FCSTD DOCUMENT  (FreeCAD 0.21R33675 (Git))
Label: Stator
License: All rights reserved
LicenseURL: http://en.wikipedia.org/wiki/All_rights_reserved
objects: App::Link×2, Spreadsheet::Sheet×1, App::Part×1
EXTERNAL_REF file=../../Master_of_Puppets.FCStd obj=Alternator
EXTERNAL_REF file=../../Master_of_Puppets.FCStd obj=Spreadsheet
EXTERNAL_REF file=Stator_ResinCast_Circular.FCStd obj=PadBody001
EXTERNAL_REF file=Stator_ResinCast_Hexagonal.FCStd obj=Body
EXTERNAL_REF file=Stator_Coils.FCStd obj=Array

FEATURE [Spreadsheet::Sheet] Spreadsheet
  cells = A1='Inputs; A2='CalculatedWindTurbineShape; B2(CalculatedWindTurbineShape)==Master_of_Puppets#Spreadsheet.CalculatedWindTurbineShape; A3='StatorThickness; B3(StatorThickness)==Master_of_Puppets#Spreadsheet.StatorThickness; A4='MechanicalClearance; B4(MechanicalClearance)==Master_of_Puppets#Spreadsheet.MechanicalClearance; A5='MagnetThickness; B5(MagnetThickness)==Master_of_Puppets#Spreadsheet.MagnetThickness; A6='RotorDiskThickness; B6(RotorDiskThickness)==Master_of_Puppets#Spreadsheet.RotorDiskThickness; A7='CoilsAngle; B7(CoilsAngle)==Master_of_Puppets#Alternator.CoilsAngle; A8='StatorResinCast; A9='CircularStatorResinCast; B9(CircularStatorResinCast)==<<Stator_ResinCast_Circular>>#<<Stator_ResinCast>>._self; A10='HexagonalStatorResinCast; B10(HexagonalStatorResinCast)==<<Stator_ResinCast_Hexagonal>>#<<Stator_ResinCast>>._self; A11='StatorResinCast; B11(StatorResinCast)==CalculatedWindTurbineShape == <<Star>> ? HexagonalStatorResinCast : CircularStatorResinCast
FEATURE [App::Link] Link  label="ResinCast"
  LinkTransform = true
  LinkedObject = -> <external Stator_ResinCast_Circular.FCStd>#PadBody001
  expr: LinkedObject = Spreadsheet.StatorResinCast
FEATURE [App::Link] Link001  label="Coils"
  LinkPlacement = pos=(0,0,0) rot=(0,0,1;0.349066rad)
  LinkTransform = true
  LinkedObject = -> <external Stator_Coils.FCStd>#Array
  Placement = pos=(0,0,0) rot=(0,0,1;0.349066rad)
  expr: .LinkPlacement.Rotation.Angle = Spreadsheet.CoilsAngle
FEATURE [App::Part] Part  label="Stator"
  Group = -> [Link001,Link]
  Origin = -> Origin

RESOLVED EXTERNAL PARTS (link-assembly join: the EXTERNAL_REF files above that resolve inside this repo's crawl, each included once):
---- part ../../Master_of_Puppets.FCStd = doc fcstd_6404554055c4 (61625 chars; too large to inline — full recipe in that document) ----
---- part Stator_Coils.FCStd = doc fcstd_bcdb5df15e52 ----
FCSTD DOCUMENT  (FreeCAD 0.21R33771 (Git))
Label: Stator_Coils
License: All rights reserved
LicenseURL: http://en.wikipedia.org/wiki/All_rights_reserved
objects: App::Link×1, Part::FeaturePython×1, Spreadsheet::Sheet×1
EXTERNAL_REF file=Stator_Coil_Triangular.FCStd obj=Body
EXTERNAL_REF file=../../Master_of_Puppets.FCStd obj=Alternator
EXTERNAL_REF file=../../Master_of_Puppets.FCStd obj=Spreadsheet
EXTERNAL_REF file=Stator_Coil.FCStd obj=Body001
EXTERNAL_REF file=Stator_Coil_Triangular_Reduced.FCStd obj=Body

FEATURE [App::Link] Link  label="Coil"
  LinkPlacement = pos=(0,99.3115,0) rot=(0,0,1;0rad)
  LinkTransform = true
  LinkedObject = -> <external Stator_Coil_Triangular.FCStd>#Body
  Placement = pos=(0,99.3115,0) rot=(0,0,1;0rad)
  expr: .LinkPlacement.Base.y = Spreadsheet.CoilY
  expr: LinkedObject = Spreadsheet.Coil
FEATURE [Part::FeaturePython] Array  label="Stator_Coils"  # Draft array (typed FeaturePython)
  AlwaysSyncPlacement = false
  Angle = 360
  ArrayType = 1
  Axis = (0,0,1)
  Base = -> Link
  Center = (0,0,0)
  Count = 9
  ExpandArray = false
  Fuse = false
  IntervalAxis = (0,0,0)
  IntervalX = (50,0,0)
  IntervalY = (0,50,0)
  IntervalZ = (0,0,50)
  NumberCircles = 1
  NumberPolar = 9
  NumberX = 2
  NumberY = 2
  NumberZ = 1
  Placement = pos=(0,0,0.1) rot=(0,0,1;0rad)
  PlacementList = 9 placements: [(0,99.3115,0),(-63.8362,76.077,0),(-97.8028,17.2453,0),(-86.0063,-49.6558,0),(-33.9665,-93.3223,0),(33.9665,-93.3223,0),(86.0063,-49.6558,0),(97.8028,17.2453,0),(63.8362,76.077,0)]
  RadialDistance = 50
  ScaleList = (9) [(1,1,1),(1,1,1),(1,1,1),(1,1,1),(1,1,1),(1,1,1),(1,1,1),(1,1,1),(1,1,1)]
  Symmetry = 1
  TangentialDistance = 25
  expr: .Placement.Base.z = Spreadsheet.ThicknessOffset / 2
  expr: NumberPolar = Spreadsheet.NumberOfCoils
FEATURE [Spreadsheet::Sheet] Spreadsheet
  cells = A1='Inputs; A2='CoilType; B2(CoilType)==Master_of_Puppets#Spreadsheet.CoilType; A3='NumberOfCoils; B3(NumberOfCoils)==Master_of_Puppets#Alternator.NumberOfCoils; A4='StatorInnerHoleRadius; B4(StatorInnerHoleRadius)==Master_of_Puppets#Alternator.StatorInnerHoleRadius; A5='DoCoilsOverlap; B5(DoCoilsOverlap)==Master_of_Puppets#Alternator.DoCoilsOverlap; A6='CoilLegWidth; B6(CoilLegWidth)==Master_of_Puppets#Spreadsheet.CoilLegWidth; A7='Coil; A8='CoilY; B8(CoilY)==StatorInnerHoleRadius + (CoilType == 3 ? CoilLegWidth : 0); C8='TODO: If we position bottom-most part of triangular coil to be aligned with x-axis in their documents. then we can remove adding the CoilLegWidth logic here.; A9='Coil; B9(Coil)==CoilType != 3 ? <<Stator_Coil>>#<<Stator_Coil>>._self : (DoCoilsOverlap == 0 ? <<Stator_Coil_Triangular>>#<<Stator_Coil>>._self : <<Stator_Coil_Triangular_Reduced>>#<<Stator_Coil>>._self); A10='Static; A11='ThicknessOffset; B11(ThicknessOffset)=0.2; C11='Duplicated in Coil
---- part Stator_ResinCast_Circular.FCStd = doc fcstd_f1e4abed5104 ----
FCSTD DOCUMENT  (FreeCAD 0.21R33771 (Git))
Label: Stator_ResinCast_Circular
License: All rights reserved
LicenseURL: http://en.wikipedia.org/wiki/All_rights_reserved
objects: Spreadsheet::Sheet×1, PartDesign::Plane×1, Sketcher::SketchObject×1, PartDesign::Pad×1, PartDesign::Mirrored×1, PartDesign::PolarPattern×1, PartDesign::MultiTransform×1, PartDesign::Body×1, Part::Refine×1
note: 9 computed .brp shape members not serialized (recipe doc carries the construction recipe); baked Part::Feature solids carry a one-line shape summary decoded from their .brp
EXTERNAL_REF file=../../Master_of_Puppets.FCStd obj=Alternator
EXTERNAL_REF file=../../Master_of_Puppets.FCStd obj=Spreadsheet

FEATURE [Spreadsheet::Sheet] Spreadsheet
  cells = A1='Inputs; A2='StatorThickness; B2='HolesRadius; C2='CalculatedWindTurbineShape; A3(StatorThickness)==Master_of_Puppets#Spreadsheet.StatorThickness; B3(HolesRadius)==Master_of_Puppets#Alternator.HolesRadius; C3(CalculatedWindTurbineShape)==Master_of_Puppets#Spreadsheet.CalculatedWindTurbineShape; A4='StatorHolesCircumradius; B4='StatorInnerHoleRadius; C4='NumberOfStatorHoles; A5(StatorHolesCircumradius)==Master_of_Puppets#Alternator.StatorHolesCircumradius; B5(StatorInnerHoleRadius)==Master_of_Puppets#Alternator.StatorInnerHoleRadius; C5(NumberOfStatorHoles)==Master_of_Puppets#Alternator.NumberOfStatorHoles; A6='EarSize; B6='EarAngle; A7(EarSize)==Master_of_Puppets#Alternator.EarSize; B7(EarAngle)==Master_of_Puppets#Alternator.EarAngle; A8='Angle; A9='TShapeAngle; B9='HShapeAngle; C9='Angle; A10(TShapeAngle)=180; B10(HShapeAngle)=45; C10(Angle)==CalculatedWindTurbineShape == <<T>> ? TShapeAngle : HShapeAngle
FEATURE [PartDesign::Plane] DatumPlane
  Length = 870.456
  MapMode = 5
  ResizeMode = 0
  Support = -> [XY_Plane001]
  Width = 870.456
FEATURE [Sketcher::SketchObject] Sketch003
  FullyConstrained = true
  MapMode = 5
  Support = -> [DatumPlane]
  expr: Constraints[10] = Spreadsheet.StatorInnerHoleRadius
  expr: Constraints[12] = Spreadsheet.EarAngle
  expr: Constraints[23] = Spreadsheet.HolesRadius
  expr: Constraints[24] = Spreadsheet.EarSize
  expr: Constraints[3] = Spreadsheet.StatorHolesCircumradius
  sketch-geometry (15):
    g0: Circle CenterX=0 CenterY=0 CenterZ=0 NormalX=0 NormalY=0 NormalZ=1 AngleXU=0 Radius=327.69
    g1: LineSegment StartX=0 StartY=0 StartZ=0 EndX=0 EndY=-327.69 EndZ=0
    g2: Circle CenterX=0 CenterY=-327.69 CenterZ=0 NormalX=0 NormalY=0 NormalZ=1 AngleXU=0 Radius=35
    g3: LineSegment StartX=-15.7387 StartY=-358.952 StartZ=0 EndX=-147.354 EndY=-292.69 EndZ=0
    g4: ArcOfCircle CenterX=0 CenterY=-327.69 CenterZ=0 NormalX=0 NormalY=0 NormalZ=1 AngleXU=0 Radius=35 StartAngle=4.24598 EndAngle=4.71239
    g5: Circle CenterX=0 CenterY=0 CenterZ=0 NormalX=0 NormalY=0 NormalZ=1 AngleXU=0 Radius=172.71
    g6: LineSegment StartX=0 StartY=0 StartZ=0 EndX=-231.712 EndY=-231.712 EndZ=0
    g7: LineSegment StartX=0 StartY=0 StartZ=0 EndX=231.712 EndY=-231.712 EndZ=0
    g8: ArcOfCircle CenterX=0 CenterY=0 CenterZ=0 NormalX=0 NormalY=0 NormalZ=1 AngleXU=0 Radius=327.69 StartAngle=3.92699 EndAngle=4.24599
    g9: ArcOfCircle CenterX=0 CenterY=0 CenterZ=0 NormalX=0 NormalY=0 NormalZ=1 AngleXU=0 Radius=172.71 StartAngle=3.92699 EndAngle=4.71239
    g10: LineSegment StartX=-231.712 StartY=-231.712 StartZ=0 EndX=-122.125 EndY=-122.125 EndZ=0
    g11: Circle CenterX=0 CenterY=-327.69 CenterZ=0 NormalX=0 NormalY=0 NormalZ=1 AngleXU=0 Radius=7
    g12: LineSegment StartX=-1.3e-15 StartY=-362.69 StartZ=0 EndX=-1.3e-15 EndY=-334.69 EndZ=0
    g13: LineSegment StartX=4e-16 StartY=-320.69 StartZ=0 EndX=4e-16 EndY=-172.71 EndZ=0
    g14: ArcOfCircle CenterX=0 CenterY=-327.69 CenterZ=0 NormalX=0 NormalY=0 NormalZ=1 AngleXU=0 Radius=7 StartAngle=1.5708 EndAngle=4.71239
  constraints (38):
    c: Coincident(g0,g-1)
    c: Coincident(g1,g-1)
    c: Vertical(g1)
    c: Radius(g0) = 327.69
    c: Coincident(g2,g1)
    c: PointOnObject(g4,g2)
    c: Tangent(g3,g2)
    c: Coincident(g4,g1)
    c: Coincident(g4,g3)
    c: Coincident(g5,g-1)
    c: Radius(g5) = 172.71
    c: PointOnObject(g4,g0)
    c: Angle(g6,g7) = 1.5708
    c: Coincident(g8,g5)
    c: Coincident(g8,g6)
    c: Coincident(g8,g3)
    c: Coincident(g9,g5)
    c: PointOnObject(g9,g6)
    c: Coincident(g7,g6)
    c: Coincident(g6,g8)
    c: Coincident(g10,g8)
    c: Coincident(g10,g9)
    c: Coincident(g11,g4)
    c: Radius(g11) = 7
    c: Radius(g2) = 35
    c: PointOnObject(g9,g1)
    c: PointOnObject(g9,g5)
    c: Symmetric(g8,g7,g1)
    c: Tangent(g3,g0) = 1.5708
    c: Coincident(g12,g4)
    c: PointOnObject(g12,g11)
    c: Vertical(g12)
    c: Coincident(g13,g9)
    c: Vertical(g13)
    c: Coincident(g14,g4)
    c: Coincident(g14,g13)
    c: Coincident(g14,g12)
    c: PointOnObject(g12,g-2)
FEATURE [PartDesign::Pad] Pad
  Direction = (0,0,1)
  Length = 14
  Length2 = 100
  Profile = -> Sketch003
  Type = 0
  expr: Length = Spreadsheet.StatorThickness
FEATURE [PartDesign::Mirrored] Mirrored
  MirrorPlane = -> Sketch003 [V_Axis]
FEATURE [PartDesign::PolarPattern] PolarPattern
  Angle = 360
  Axis = -> Z_Axis001
  Occurrences = 4
  expr: Occurrences = Spreadsheet.NumberOfStatorHoles
FEATURE [PartDesign::MultiTransform] MultiTransform
  BaseFeature = -> Pad
  Originals = -> [Pad]
  Transformations = -> [Mirrored,PolarPattern]
FEATURE [PartDesign::Body] PadBody  label="Body"
  Group = -> [DatumPlane,Sketch003,Pad,MultiTransform,Mirrored,PolarPattern]
  Origin = -> Origin001
  Tip = -> MultiTransform
FEATURE [Part::Refine] PadBody001  label="Stator_ResinCast"
  Placement = pos=(0,0,0) rot=(0,0,1;0.785398rad)
  Source = -> PadBody
  expr: .Placement.Rotation.Angle = Spreadsheet.Angle
---- part Stator_ResinCast_Hexagonal.FCStd = doc fcstd_1f7028579323 ----
FCSTD DOCUMENT  (FreeCAD 0.20R29177 (Git))
Label: Stator_ResinCast_Hexagonal
License: All rights reserved
LicenseURL: http://en.wikipedia.org/wiki/All_rights_reserved
objects: Sketcher::SketchObject×3, PartDesign::Pocket×2, PartDesign::Pad×1, Spreadsheet::Sheet×1, PartDesign::Body×1
note: 10 computed .brp shape members not serialized (recipe doc carries the construction recipe); baked Part::Feature solids carry a one-line shape summary decoded from their .brp
EXTERNAL_REF file=../../Master_of_Puppets.FCStd obj=Alternator
EXTERNAL_REF file=../../Master_of_Puppets.FCStd obj=Spreadsheet

FEATURE [Sketcher::SketchObject] Sketch
  FullyConstrained = true
  MapMode = 5
  Support = -> [XY_Plane]
  expr: Constraints[1] = Spreadsheet.StatorInnerHoleRadius
  expr: Constraints[20] = Spreadsheet.StatorOuterCircle
  sketch-geometry (8):
    g0: Circle CenterX=0 CenterY=0 CenterZ=0 NormalX=0 NormalY=0 NormalZ=1 AngleXU=0 Radius=81.7481
    g1: LineSegment StartX=110.563 StartY=191.5 StartZ=0 EndX=-110.563 EndY=191.5 EndZ=0
    g2: LineSegment StartX=-110.563 StartY=191.5 StartZ=0 EndX=-221.125 EndY=0 EndZ=0
    g3: LineSegment StartX=-221.125 StartY=0 StartZ=0 EndX=-110.563 EndY=-191.5 EndZ=0
    g4: LineSegment StartX=-110.563 StartY=-191.5 StartZ=0 EndX=110.563 EndY=-191.5 EndZ=0
    g5: LineSegment StartX=110.563 StartY=-191.5 StartZ=0 EndX=221.125 EndY=-2.84e-14 EndZ=0
    g6: LineSegment StartX=221.125 StartY=-2.84e-14 StartZ=0 EndX=110.563 EndY=191.5 EndZ=0
    g7: Circle CenterX=0 CenterY=0 CenterZ=0 NormalX=0 NormalY=0 NormalZ=1 AngleXU=0 Radius=221.125
  constraints (18):
    c: Coincident(g0,g-1)
    c: Radius(g0) = 81.7481
    c: Coincident(g1,g2)
    c: Coincident(g2,g3)
    c: Coincident(g3,g4)
    c: Coincident(g4,g5)
    c: Coincident(g5,g6)
    c: Coincident(g6,g1)
    c: Equal(g1, g2-g6) x5
    c: PointOnObject(g1,g7)
    c: PointOnObject(g2,g7)
    c: PointOnObject(g3,g7)
    c: PointOnObject(g4,g7)
    c: PointOnObject(g5,g7)
    c: PointOnObject(g6,g7)
    c: Coincident(g7,g-1)
    c: Radius(g7) = 221.125
    c: Horizontal(g1)
FEATURE [PartDesign::Pad] Pad
  AllowMultiFace = false
  Direction = (0,0,1)
  Length = 13
  Length2 = 100
  Profile = -> Sketch
  Type = 0
  expr: Length = Spreadsheet.StatorThickness
FEATURE [Spreadsheet::Sheet] Spreadsheet
  cells = A1=Inputs; A2=RotorRadius; B2(RotorDiskRadius)==Master_of_Puppets#Spreadsheet.RotorDiskRadius; A3=MagnetLength; B3(MagnetLength)==Master_of_Puppets#Spreadsheet.MagnetLength; A4=CoilLegWidth; B4(CoilLegWidth)==Master_of_Puppets#Spreadsheet.CoilLegWidth; A5=HolesRadius; B5(HolesRadius)==Master_of_Puppets#Alternator.HolesRadius; A6=StatorThickness; B6(StatorThickness)==Master_of_Puppets#Spreadsheet.StatorThickness; A7=HexagonalStatorOuterCircumradius; B7(StatorOuterCircle)==Master_of_Puppets#Alternator.HexagonalStatorOuterCircumradius; A8=StatorHolesCircumradius; B8(StatorHolesCircumradius)==Master_of_Puppets#Alternator.StatorHolesCircumradius; A9=StatorInnerHoleRadius; B9(StatorInnerHoleRadius)==Master_of_Puppets#Alternator.StatorInnerHoleRadius
FEATURE [Sketcher::SketchObject] Sketch001
  ExternalGeometry = -> [Pad]
  FullyConstrained = true
  MapMode = 5
  Placement = pos=(0,0,13) rot=(0,0,1;0rad)
  Support = -> [Pad]
  expr: Constraints[0] = Spreadsheet.StatorHolesCircumradius
  expr: Constraints[13] = Spreadsheet.HolesRadius
  expr: Constraints[14] = Spreadsheet.HolesRadius
  expr: Constraints[15] = Spreadsheet.HolesRadius
  expr: Constraints[1] = Spreadsheet.HolesRadius
  sketch-geometry (8):
    g0: Circle CenterX=95.75 CenterY=165.844 CenterZ=0 NormalX=0 NormalY=0 NormalZ=1 AngleXU=0 Radius=6
    g1: Circle CenterX=0 CenterY=0 CenterZ=0 NormalX=0 NormalY=0 NormalZ=1 AngleXU=0 Radius=191.5
    g2: Circle CenterX=-95.75 CenterY=165.844 CenterZ=0 NormalX=0 NormalY=0 NormalZ=1 AngleXU=0 Radius=6
    g3: Circle CenterX=-95.75 CenterY=-165.844 CenterZ=0 NormalX=0 NormalY=0 NormalZ=1 AngleXU=0 Radius=6
    g4: LineSegment StartX=-95.75 StartY=165.844 StartZ=0 EndX=-95.75 EndY=-165.844 EndZ=0
    g5: Circle CenterX=95.75 CenterY=-165.844 CenterZ=0 NormalX=0 NormalY=0 NormalZ=1 AngleXU=0 Radius=6
    g6: LineSegment StartX=95.75 StartY=-165.844 StartZ=0 EndX=95.75 EndY=165.844 EndZ=0
    g7: LineSegment StartX=0 StartY=0 StartZ=0 EndX=110.563 EndY=191.5 EndZ=0
  constraints (19):
    c: Radius(g1) = 191.5
    c: Radius(g0) = 6
    c: PointOnObject(g0,g1)
    c: Coincident(g1,g-1)
    c: Symmetric(g2,g0,g-2)
    c: PointOnObject(g3,g1)
    c: Coincident(g4,g2)
    c: Coincident(g4,g3)
    c: Vertical(g4)
    c: PointOnObject(g5,g1)
    c: Coincident(g6,g5)
    c: Coincident(g6,g0)
    c: Vertical(g6)
    c: Radius(g5) = 6
    c: Radius(g3) = 6
    c: Radius(g2) = 6
    c: Coincident(g7,g-1)
    c: Coincident(g7,g-4)
    c: PointOnObject(g0,g7)
FEATURE [PartDesign::Pocket] Pocket
  AllowMultiFace = false
  BaseFeature = -> Pad
  Direction = (0,0,-1)
  Length = 5
  Length2 = 100
  Profile = -> Sketch001
  Type = 1
FEATURE [Sketcher::SketchObject] Sketch002
  ExternalGeometry = -> [Pocket]
  FullyConstrained = false
  MapMode = 5
  Placement = pos=(0,0,13) rot=(0,0,1;0rad)
  Support = -> [Pocket]
  expr: Constraints[2] = Spreadsheet.HolesRadius
  expr: Constraints[6] = Spreadsheet.HolesRadius
  expr: Constraints[7] = Spreadsheet.StatorHolesCircumradius
  sketch-geometry (4):
    g0: Circle CenterX=0 CenterY=0 CenterZ=0 NormalX=0 NormalY=0 NormalZ=1 AngleXU=0 Radius=191.5
    g1: Circle CenterX=-191.5 CenterY=0 CenterZ=0 NormalX=0 NormalY=0 NormalZ=1 AngleXU=0 Radius=6
    g2: Circle CenterX=191.5 CenterY=0 CenterZ=0 NormalX=0 NormalY=0 NormalZ=1 AngleXU=0 Radius=6
    g3: LineSegment StartX=-453.104 StartY=0 StartZ=0 EndX=453.104 EndY=0 EndZ=0
  constraints (8):
    c: Coincident(g0,g-1)
    c: PointOnObject(g1,g0)
    c: Radius(g1) = 6
    c: PointOnObject(g2,g0)
    c: PointOnObject(g2,g3)
    c: PointOnObject(g1,g3)
    c: Radius(g2) = 6
    c: Radius(g0) = 191.5
FEATURE [PartDesign::Pocket] Pocket001
  AllowMultiFace = false
  BaseFeature = -> Pocket
  Direction = (0,0,-1)
  Length = 5
  Length2 = 100
  Profile = -> Sketch002
  Type = 1
FEATURE [PartDesign::Body] Body  label="Stator_ResinCast"
  Group = -> [Sketch,Pad,Sketch001,Pocket,Sketch002,Pocket001]
  Origin = -> Origin
  Tip = -> Pocket001
